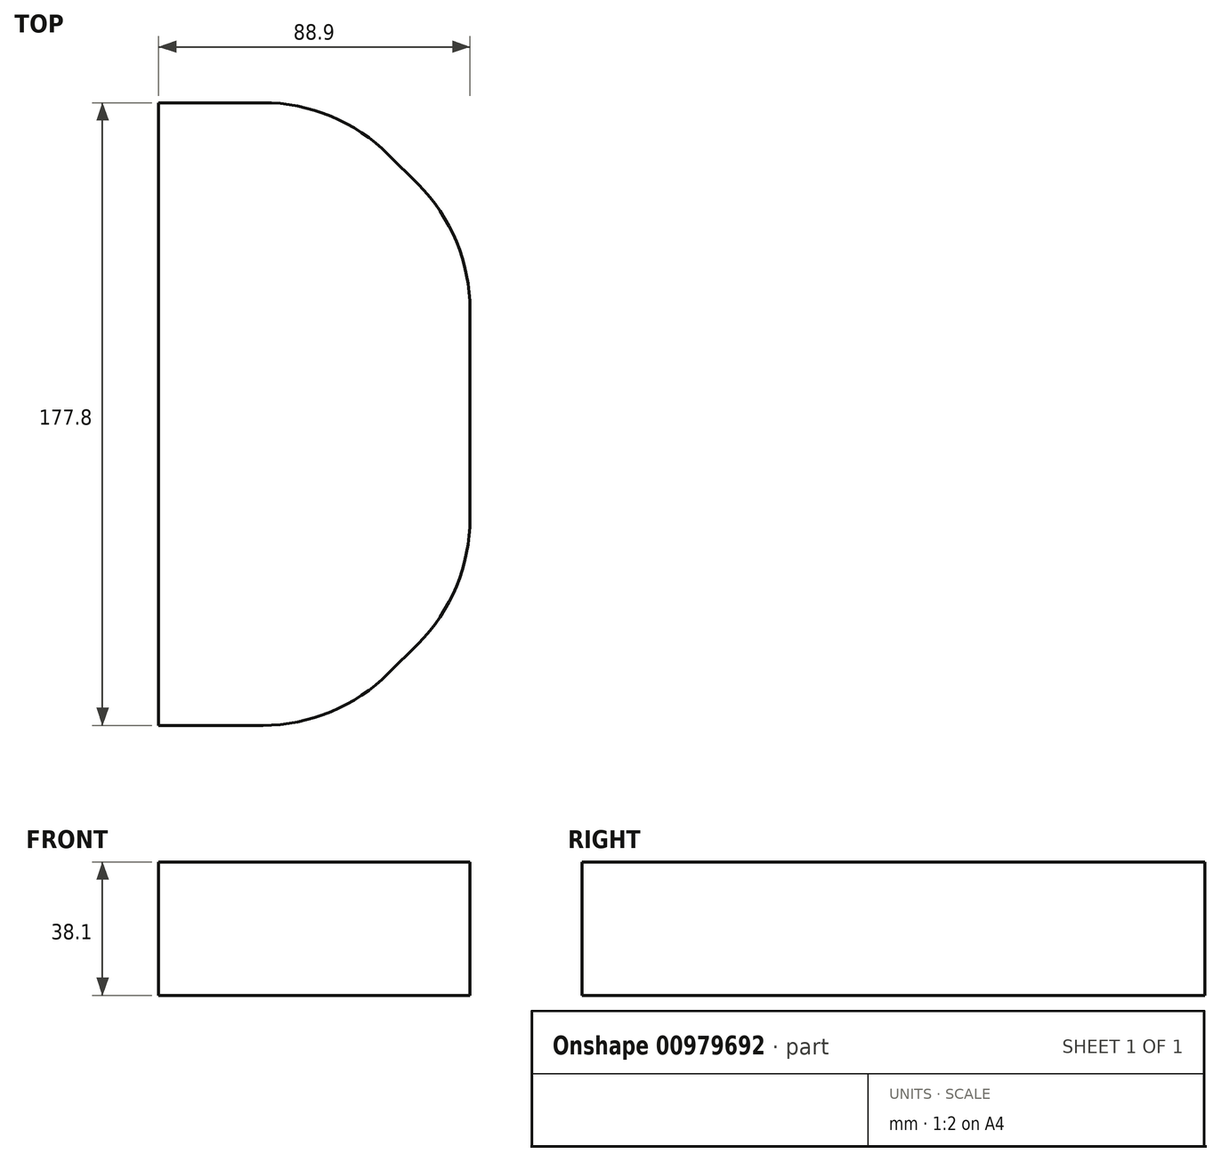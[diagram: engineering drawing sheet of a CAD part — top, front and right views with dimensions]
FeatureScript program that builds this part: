
annotation { "Feature Type Name" : "Feature", "Feature Type Description" : "" }
export const myFeature = defineFeature(function(context is Context, id is Id, definition is map)
    precondition{}
    {
        {
            var Q0;
            Q0=qCreatedBy(makeId("Top.planeOp"),FACE);
            var sketch = newSketch(context, id + "F0", { "sketchPlane" : qUnion([Q0])});
            skLineSegment(sketch, "E0", {"start": v(0, 0) * mm, "end": v(88.9, 0) * mm});
            skLineSegment(sketch, "E1", {"start": v(74.02, 65.68) * mm, "end": v(65.68, 74.02) * mm});
            skLineSegment(sketch, "E2", {"start": v(0, 88.9) * mm, "end": v(0, 0) * mm});
            skLineSegment(sketch, "E3", {"start": v(88.9, 0) * mm, "end": v(88.9, 29.76) * mm});
            skLineSegment(sketch, "E4", {"start": v(0, 88.9) * mm, "end": v(29.76, 88.9) * mm});
            skPoint(sketch, "E5.orphan", {"position": v(0, 139.7) * mm});
            skPoint(sketch, "E6.visualSharp", {"position": v(50.8, 88.9) * mm});
            skArc(sketch, "E6.filletArc", {"start": v(65.68, 74.02) * mm, "mid": v(49.2, 85.03) * mm, "end": v(29.76, 88.9) * mm});
            skPoint(sketch, "E7.visualSharp", {"position": v(88.9, 50.8) * mm});
            skArc(sketch, "E7.filletArc", {"start": v(88.9, 29.76) * mm, "mid": v(85.03, 49.2) * mm, "end": v(74.02, 65.68) * mm});
            skLineSegment(sketch, "E8.MirrorCS", {"start": v(74.02, -65.68) * mm, "end": v(65.68, -74.02) * mm});
            skLineSegment(sketch, "E9.MirrorCS", {"start": v(0, -88.9) * mm, "end": v(29.76, -88.9) * mm});
            skPoint(sketch, "E10.MirrorP", {"position": v(88.9, -50.8) * mm});
            skLineSegment(sketch, "E11.MirrorCS", {"start": v(88.9, 0) * mm, "end": v(88.9, -29.76) * mm});
            skArc(sketch, "E12.MirrorCS", {"start": v(65.68, -74.02) * mm, "mid": v(49.2, -85.03) * mm, "end": v(29.76, -88.9) * mm});
            skLineSegment(sketch, "E13.MirrorCS", {"start": v(0, -88.9) * mm, "end": v(0, 0) * mm});
            skArc(sketch, "E14.MirrorCS", {"start": v(88.9, -29.76) * mm, "mid": v(85.03, -49.2) * mm, "end": v(74.02, -65.68) * mm});
            skPoint(sketch, "E15.MirrorP", {"position": v(50.8, -88.9) * mm});
            skSolve(sketch);
        }
        {
            var Q0;
            Q0 = qSketchRegion(id + "F0", true);
            extrude(context, id + "F1", {"entities" : qUnion([Q0]), "depth" : 38.1 * mm, "offsetDistance" : 25.4 * mm});
        }
    });
